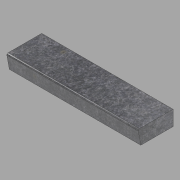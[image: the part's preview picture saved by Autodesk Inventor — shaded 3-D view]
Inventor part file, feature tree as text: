
AUTODESK INVENTOR PART (.ipt)
format: ipt  version: 2022.1 (Build 261234020, 234B)  size: 98,816 bytes
history: native  units: in
note: dims shown in document units (in); Inventor stores cm internally (conversion verified against a paired STEP export)
features: other x3, extrude x1, sketch x1
ambient origin geometry x8: Origin, YZ Plane, XZ Plane, XY Plane, X Axis, Y Axis, Z Axis, Center Point
bodies: Solid1 (feature_tree)
feature tree (5):
  other  "Blocks"
  extrude  "Extrusion1"  Depth=52.8281in TaperAngle=0.0deg
  sketch  "Sketch1"  dims[d0=13.0in d1=6.0in d2=13.5in d3=0.5in d4=0.5in d5=52.8281in d6=0.0in]
  other  "Profile"
  other  "Profile:1"
